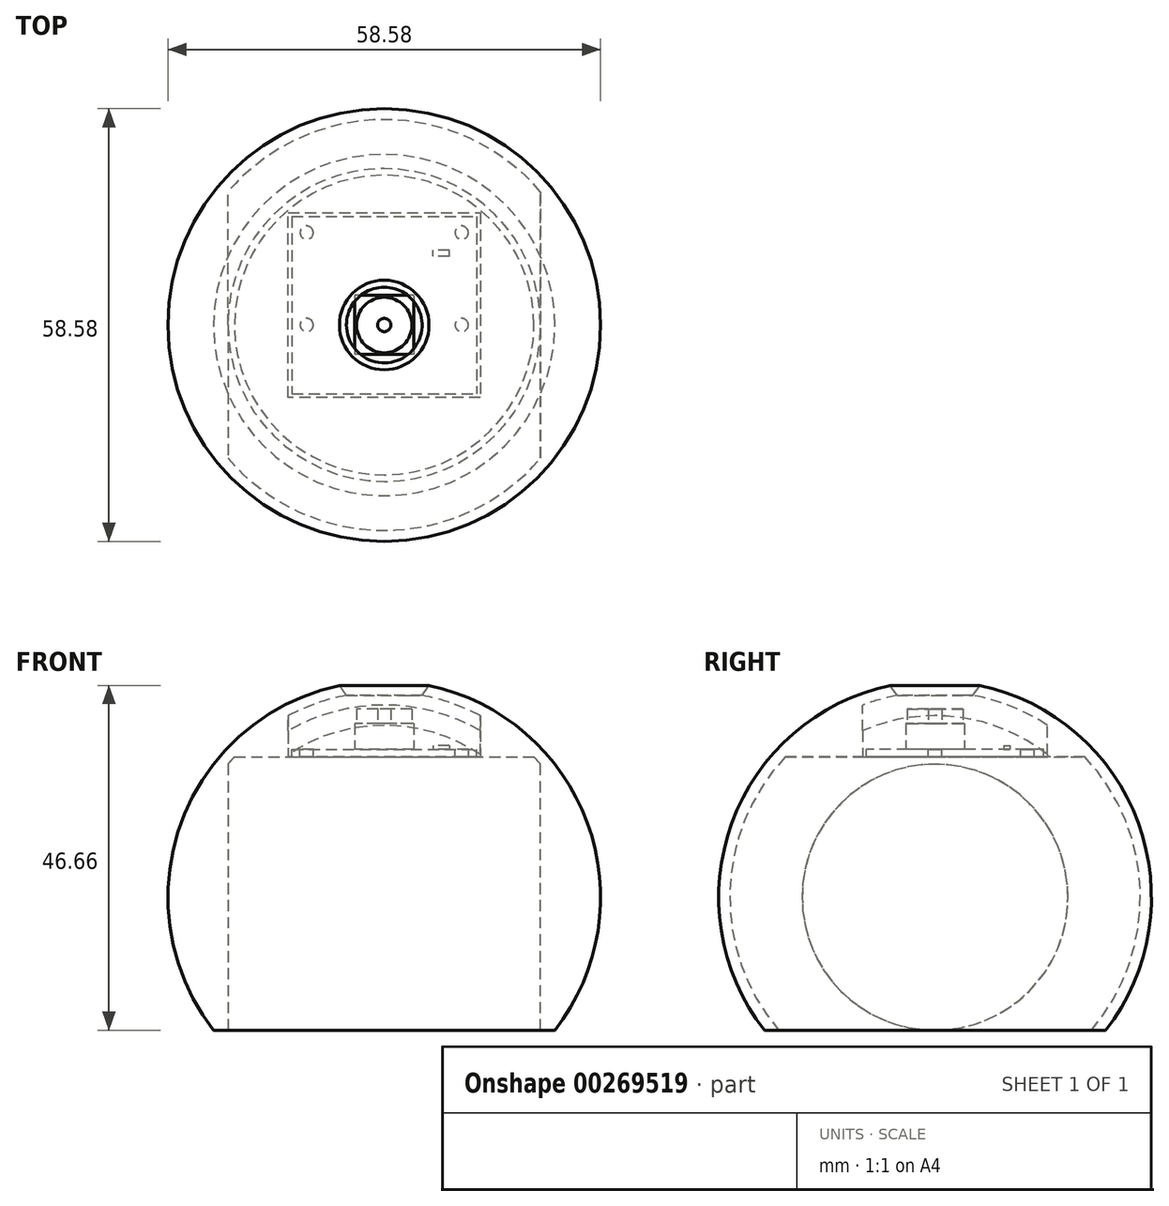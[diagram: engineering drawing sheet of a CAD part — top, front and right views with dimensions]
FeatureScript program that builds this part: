
annotation { "Feature Type Name" : "Feature", "Feature Type Description" : "" }
export const myFeature = defineFeature(function(context is Context, id is Id, definition is map)
    precondition{}
    {
        {
            var Q0;
            Q0=qCreatedBy(makeId("Top.planeOp"),FACE);
            var sketch = newSketch(context, id + "F0", { "sketchPlane" : qUnion([Q0])});
            skLineSegment(sketch, "E0.bottom", {"start": v(-10.5, 0) * mm, "end": v(10.5, 0) * mm, "construction": true});
            skLineSegment(sketch, "E0.top", {"start": v(-10.5, 12.5) * mm, "end": v(10.5, 12.5) * mm, "construction": true});
            skLineSegment(sketch, "E0.left", {"start": v(-10.5, 0) * mm, "end": v(-10.5, 12.5) * mm, "construction": true});
            skLineSegment(sketch, "E0.right", {"start": v(10.5, 0) * mm, "end": v(10.5, 12.5) * mm, "construction": true});
            skCircle(sketch, "E1", {"center": v(-10.5, 0) * mm, "radius": 0.9 * mm});
            skCircle(sketch, "E2", {"center": v(-10.5, 12.5) * mm, "radius": 0.9 * mm});
            skCircle(sketch, "E3", {"center": v(10.5, 12.5) * mm, "radius": 0.9 * mm});
            skCircle(sketch, "E4", {"center": v(10.5, 0) * mm, "radius": 0.9 * mm});
            skLineSegment(sketch, "E5.bottom", {"start": v(-12.5, 14.7) * mm, "end": v(12.5, 14.7) * mm});
            skLineSegment(sketch, "E5.top", {"start": v(-12.5, -9.3) * mm, "end": v(12.5, -9.3) * mm});
            skLineSegment(sketch, "E5.left", {"start": v(-12.5, 14.7) * mm, "end": v(-12.5, -9.3) * mm});
            skLineSegment(sketch, "E5.right", {"start": v(12.5, 14.7) * mm, "end": v(12.5, -9.3) * mm});
            skLineSegment(sketch, "E6.bottom", {"start": v(4, 4) * mm, "end": v(-4, 4) * mm});
            skLineSegment(sketch, "E6.top", {"start": v(4, -4) * mm, "end": v(-4, -4) * mm});
            skLineSegment(sketch, "E6.left", {"start": v(4, 4) * mm, "end": v(4, -4) * mm});
            skLineSegment(sketch, "E6.right", {"start": v(-4, 4) * mm, "end": v(-4, -4) * mm});
            skPoint(sketch, "E6.middle", {"position": v(0, 0) * mm});
            skLineSegment(sketch, "E7.bottom", {"start": v(8.8, 9.3) * mm, "end": v(6.6, 9.3) * mm});
            skLineSegment(sketch, "E7.top", {"start": v(8.8, 10.1) * mm, "end": v(6.6, 10.1) * mm});
            skLineSegment(sketch, "E7.left", {"start": v(8.8, 9.3) * mm, "end": v(8.8, 10.1) * mm});
            skLineSegment(sketch, "E7.right", {"start": v(6.6, 9.3) * mm, "end": v(6.6, 10.1) * mm});
            skPoint(sketch, "E7.middle", {"position": v(7.7, 9.7) * mm});
            skCircle(sketch, "E8", {"center": v(0, 0) * mm, "radius": 19.3 * mm, "construction": true});
            skSolve(sketch);
        }
        {
            var Q0;
            Q0=makeQuery(id+"F0.imprint","IMPRINT",FACE,{"disambiguationData":[TD([[makeQuery(id+"F0.imprint","IMPRINT",EDGE,{"derivedFrom":sQuery(id+"F0.wireOp",EDGE,"E1")}),-1.0]])]});
            var Q1;
            Q1=makeQuery(id+"F0.imprint","IMPRINT",FACE,{"disambiguationData":[TD([[makeQuery(id+"F0.imprint","IMPRINT",EDGE,{"derivedFrom":sQuery(id+"F0.wireOp",EDGE,"E6.bottom")}),1.0]])]});
            var Q2;
            Q2=makeQuery(id+"F0.imprint","IMPRINT",FACE,{"disambiguationData":[TD([[makeQuery(id+"F0.imprint","IMPRINT",EDGE,{"derivedFrom":sQuery(id+"F0.wireOp",EDGE,"E7.bottom")}),-1.0]])]});
            extrude(context, id + "F1", {"entities" : qUnion([Q0, Q1, Q2]), "oppositeDirection" : true, "depth" : 1 * mm});
        }
        {
            var Q0;
            Q0=makeQuery(id+"F0.imprint","IMPRINT",FACE,{"disambiguationData":[TD([[makeQuery(id+"F0.imprint","IMPRINT",EDGE,{"derivedFrom":sQuery(id+"F0.wireOp",EDGE,"E6.bottom")}),1.0]])]});
            extrude(context, id + "F2", {"entities" : qUnion([Q0]), "operationType" : NewBodyOperationType.ADD, "depth" : 3.5 * mm});
        }
        {
            var Q0;
            Q0=makeQuery(id+"F0.imprint","IMPRINT",FACE,{"disambiguationData":[TD([[makeQuery(id+"F0.imprint","IMPRINT",EDGE,{"derivedFrom":sQuery(id+"F0.wireOp",EDGE,"E7.bottom")}),-1.0]])]});
            extrude(context, id + "F3", {"entities" : qUnion([Q0]), "operationType" : NewBodyOperationType.ADD, "depth" : 0.5 * mm});
        }
        {
            var Q0;
            Q0=makeQuery(id+"F2.opExtrude","CAP_FACE",FACE,{"disambiguationData":[OSD([sQuery(id+"F0.wireOp",EDGE,"E6.bottom"),sQuery(id+"F0.wireOp",EDGE,"E6.top"),sQuery(id+"F0.wireOp",EDGE,"E6.left"),sQuery(id+"F0.wireOp",EDGE,"E6.right")])],"isStart":false});
            var sketch = newSketch(context, id + "F4", { "sketchPlane" : qUnion([Q0])});
            skCircle(sketch, "E9", {"center": v(0, 0) * mm, "radius": 3.75 * mm});
            skCircle(sketch, "E10", {"center": v(0, 0) * mm, "radius": 0.9 * mm});
            skSolve(sketch);
        }
        {
            var Q0;
            Q0=makeQuery(id+"F4.imprint","IMPRINT",FACE,{"disambiguationData":[TD([[makeQuery(id+"F4.imprint","IMPRINT",EDGE,{"derivedFrom":sQuery(id+"F4.wireOp",EDGE,"E9")}),1.0]])]});
            extrude(context, id + "F5", {"entities" : qUnion([Q0]), "operationType" : NewBodyOperationType.ADD, "depth" : 2 * mm});
        }
        {
            var Q0;
            Q0=qCreatedBy(makeId("Right.planeOp"),FACE);
            var sketch = newSketch(context, id + "F6", { "sketchPlane" : qUnion([Q0])});
            skLineSegment(sketch, "E11.0", {"start": v(-19.3, 0) * mm, "end": v(19.3, 0) * mm, "construction": true});
            skArc(sketch, "E12", {"start": v(21.17, -38) * mm, "mid": v(26.2, -10.72) * mm, "end": v(5.12, 7.31) * mm});
            skArc(sketch, "E13", {"start": v(23.1, -38) * mm, "mid": v(27.51, -9.95) * mm, "end": v(6.06, 8.66) * mm});
            skLineSegment(sketch, "E14", {"start": v(0, -38) * mm, "end": v(21.17, -38) * mm, "construction": true});
            skLineSegment(sketch, "E15", {"start": v(21.17, -38) * mm, "end": v(23.1, -38) * mm});
            skLineSegment(sketch, "E16", {"start": v(0, 0) * mm, "end": v(5.12, 7.31) * mm, "construction": true});
            skLineSegment(sketch, "E17", {"start": v(5.12, 7.31) * mm, "end": v(6.06, 8.66) * mm});
            skLineSegment(sketch, "E18", {"start": v(0, -20) * mm, "end": v(0, 0) * mm, "construction": true});
            skSolve(sketch);
        }
        {
            var Q0;
            Q0 = qSketchRegion(id + "F6", true);
            var Q1;
            Q1=sQuery(id+"F6.wireOp",EDGE,"E18");
            revolve(context, id + "F7", {"entities" : qUnion([Q0]), "axis" : qUnion([Q1]), "revolveType" : RevolveType.FULL});
        }
        {
            var Q0;
            Q0=makeQuery(id+"F1.opExtrude","CAP_FACE",FACE,{"disambiguationData":[OSD([sQuery(id+"F0.wireOp",EDGE,"E1"),sQuery(id+"F0.wireOp",EDGE,"E2"),sQuery(id+"F0.wireOp",EDGE,"E3"),sQuery(id+"F0.wireOp",EDGE,"E4"),sQuery(id+"F0.wireOp",EDGE,"E5.bottom"),sQuery(id+"F0.wireOp",EDGE,"E5.top"),sQuery(id+"F0.wireOp",EDGE,"E5.left"),sQuery(id+"F0.wireOp",EDGE,"E5.right")])],"isStart":false});
            var sketch = newSketch(context, id + "F8", { "sketchPlane" : qUnion([Q0])});
            skLineSegment(sketch, "E19.0.0", {"start": v(-12.5, 9.3) * mm, "end": v(-12.5, -14.7) * mm, "construction": true});
            skLineSegment(sketch, "E19.0.1", {"start": v(-12.5, -14.7) * mm, "end": v(12.5, -14.7) * mm, "construction": true});
            skLineSegment(sketch, "E19.0.2", {"start": v(12.5, -14.7) * mm, "end": v(12.5, 9.3) * mm, "construction": true});
            skLineSegment(sketch, "E19.0.3", {"start": v(12.5, 9.3) * mm, "end": v(-12.5, 9.3) * mm, "construction": true});
            skCircle(sketch, "E20", {"center": v(0, 0) * mm, "radius": 20.28 * mm});
            skLineSegment(sketch, "E21.0", {"start": v(-13, 9.8) * mm, "end": v(-13, -15.2) * mm});
            skLineSegment(sketch, "E21.1", {"start": v(13, 9.8) * mm, "end": v(-13, 9.8) * mm});
            skLineSegment(sketch, "E21.2", {"start": v(13, -15.2) * mm, "end": v(13, 9.8) * mm});
            skLineSegment(sketch, "E21.3", {"start": v(-13, -15.2) * mm, "end": v(13, -15.2) * mm});
            skSolve(sketch);
        }
        {
            var Q0;
            Q0=makeQuery(id+"F8.imprint","IMPRINT",FACE,{"disambiguationData":[TD([[makeQuery(id+"F8.imprint","IMPRINT",EDGE,{"derivedFrom":sQuery(id+"F8.wireOp",EDGE,"E20")}),1.0]])]});
            extrude(context, id + "F9", {"entities" : qUnion([Q0]), "operationType" : NewBodyOperationType.ADD, "endBound" : BoundingType.UP_TO_NEXT, "oppositeDirection" : true, "depth" : 25 * mm});
        }
        {
            var Q0;
            Q0=qCreatedBy(makeId("Front.planeOp"),FACE);
            var sketch = newSketch(context, id + "F10", { "sketchPlane" : qUnion([Q0])});
            skArc(sketch, "E22", {"start": v(-6.06, 8.66) * mm, "mid": v(-27.51, -9.95) * mm, "end": v(-23.1, -38) * mm});
            skArc(sketch, "E23", {"start": v(23.1, -38) * mm, "mid": v(27.51, -9.95) * mm, "end": v(6.06, 8.66) * mm});
            skArc(sketch, "E24", {"start": v(-20.28, -1) * mm, "mid": v(-27.78, -19.33) * mm, "end": v(-21.17, -38) * mm});
            skArc(sketch, "E25", {"start": v(21.17, -38) * mm, "mid": v(27.78, -19.33) * mm, "end": v(20.28, -1) * mm});
            skLineSegment(sketch, "E26", {"start": v(-21.17, -38) * mm, "end": v(-21.17, -20) * mm, "construction": true});
            skLineSegment(sketch, "E27", {"start": v(-21.17, -20) * mm, "end": v(0, -20) * mm, "construction": true});
            skLineSegment(sketch, "E28", {"start": v(21.17, -38) * mm, "end": v(21.17, -20) * mm, "construction": true});
            skLineSegment(sketch, "E29", {"start": v(21.17, -20) * mm, "end": v(0, -20) * mm, "construction": true});
            skSolve(sketch);
        }
        {
            var Q0;
            Q0=sQuery(id+"F10.wireOp",EDGE,"E26");
            cPlane(context, id + "F11", {"entities" : qUnion([Q0]), "cplaneType" : CPlaneType.LINE_ANGLE, "offset" : 25 * mm, "angle" : 0 * degree, "width" : 150 * mm, "height" : 150 * mm});
        }
        {
            var Q0;
            Q0=qCreatedBy(id+"F11.planeOp",FACE);
            var sketch = newSketch(context, id + "F12", { "sketchPlane" : qUnion([Q0])});
            skPoint(sketch, "E30.0", {"position": v(0, -20) * mm});
            skPoint(sketch, "E31.0", {"position": v(0, -38) * mm});
            skCircle(sketch, "E32", {"center": v(0, -20) * mm, "radius": 18 * mm});
            skCircle(sketch, "E33", {"center": v(0, -20) * mm, "radius": 1.5 * mm});
            skSolve(sketch);
        }
        {
            var Q0;
            Q0=makeQuery(id+"F12.imprint","IMPRINT",FACE,{"disambiguationData":[TD([[makeQuery(id+"F12.imprint","IMPRINT",EDGE,{"derivedFrom":sQuery(id+"F12.wireOp",EDGE,"E32")}),1.0]])]});
            var Q1;
            Q1=makeQuery(id+"F12.imprint","IMPRINT",FACE,{"disambiguationData":[TD([[makeQuery(id+"F12.imprint","IMPRINT",EDGE,{"derivedFrom":sQuery(id+"F12.wireOp",EDGE,"E33")}),1.0]])]});
            extrude(context, id + "F13", {"entities" : qUnion([Q0, Q1]), "operationType" : NewBodyOperationType.ADD, "endBound" : BoundingType.UP_TO_NEXT, "oppositeDirection" : true, "depth" : 25 * mm});
        }
        {
            var Q0;
            Q0=sQuery(id+"F10.wireOp",EDGE,"E28");
            cPlane(context, id + "F14", {"entities" : qUnion([Q0]), "cplaneType" : CPlaneType.LINE_ANGLE, "offset" : 25 * mm, "angle" : 0 * degree, "width" : 150 * mm, "height" : 150 * mm});
        }
        {
            var Q0;
            Q0=qCreatedBy(id+"F14.planeOp",FACE);
            var sketch = newSketch(context, id + "F15", { "sketchPlane" : qUnion([Q0])});
            skPoint(sketch, "E34.0", {"position": v(0, -20) * mm});
            skPoint(sketch, "E35.0", {"position": v(0, -38) * mm});
            skCircle(sketch, "E36", {"center": v(0, -20) * mm, "radius": 18 * mm});
            skSolve(sketch);
        }
        {
            var Q0;
            Q0=makeQuery(id+"F15.imprint","IMPRINT",FACE,{"disambiguationData":[TD([[makeQuery(id+"F15.imprint","IMPRINT",EDGE,{"derivedFrom":sQuery(id+"F15.wireOp",EDGE,"E36")}),1.0]])]});
            extrude(context, id + "F16", {"entities" : qUnion([Q0]), "operationType" : NewBodyOperationType.ADD, "endBound" : BoundingType.UP_TO_NEXT, "depth" : 25 * mm});
        }
    });
